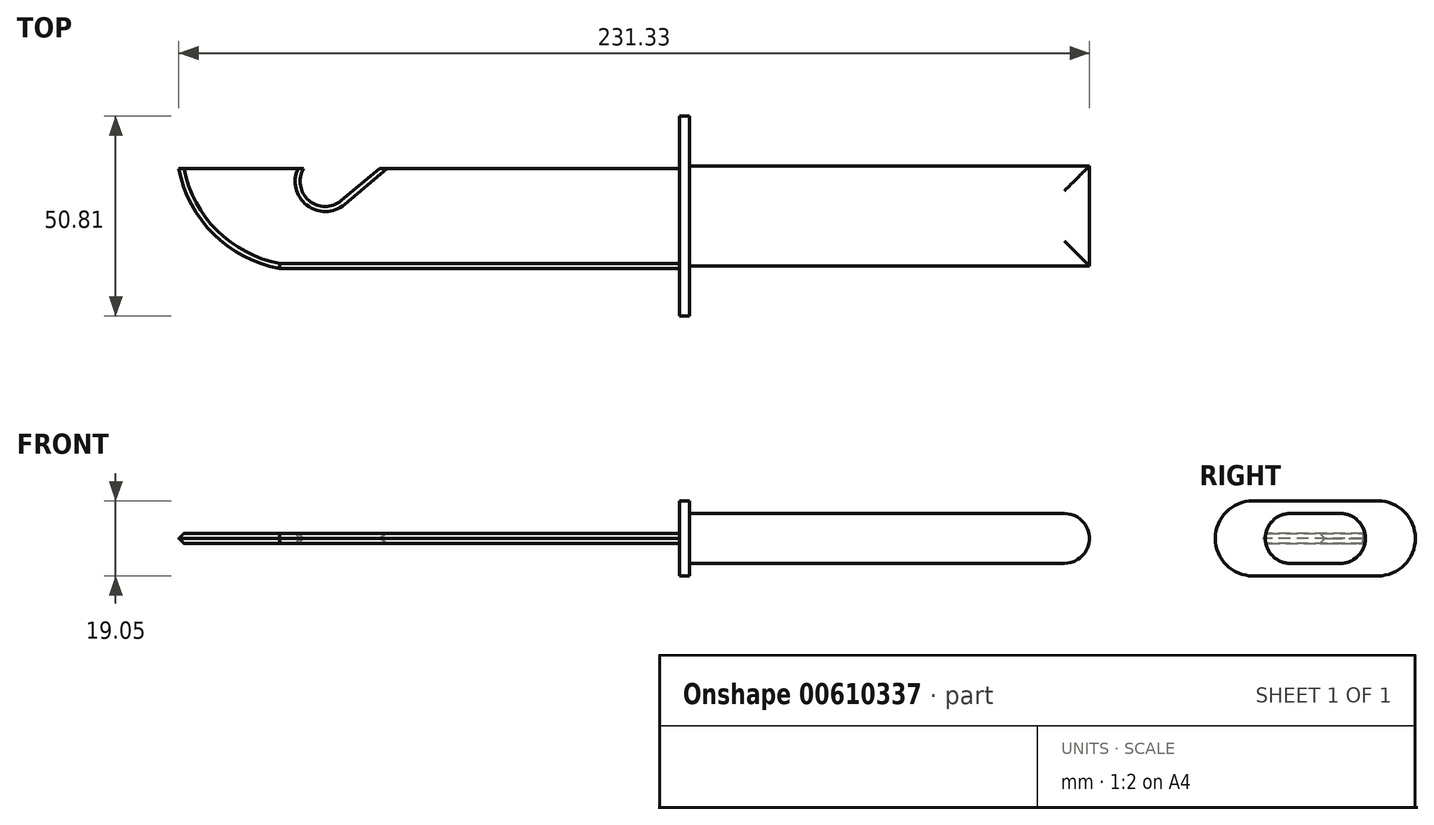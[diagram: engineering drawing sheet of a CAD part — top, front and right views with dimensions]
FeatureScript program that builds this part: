
annotation { "Feature Type Name" : "Feature", "Feature Type Description" : "" }
export const myFeature = defineFeature(function(context is Context, id is Id, definition is map)
    precondition{}
    {
        {
            var Q0;
            Q0=qCreatedBy(makeId("Top.planeOp"),FACE);
            var sketch = newSketch(context, id + "F0", { "sketchPlane" : qUnion([Q0])});
            skLineSegment(sketch, "E0", {"start": v(0, 0) * mm, "end": v(31.75, 0) * mm});
            skArc(sketch, "E1", {"start": v(31.75, 0) * mm, "mid": v(33.04, -8.12) * mm, "end": v(41.26, -8.16) * mm});
            skLineSegment(sketch, "E2", {"start": v(41.26, -8.16) * mm, "end": v(50.99, 0) * mm});
            skArc(sketch, "E3", {"start": v(0, 0) * mm, "mid": v(8.84, -16.68) * mm, "end": v(25.59, -25.4) * mm});
            skLineSegment(sketch, "E4", {"start": v(25.59, -25.4) * mm, "end": v(127.19, -25.4) * mm});
            skLineSegment(sketch, "E5", {"start": v(127.19, -25.4) * mm, "end": v(127.19, 0) * mm});
            skLineSegment(sketch, "E6", {"start": v(127.19, 0) * mm, "end": v(50.99, 0) * mm});
            skSolve(sketch);
        }
        {
            var Q0;
            Q0 = qSketchRegion(id + "F0", true);
            extrude(context, id + "F1", {"entities" : qUnion([Q0]), "depth" : 2.54 * mm, "offsetDistance" : 25.4 * mm});
        }
        {
            var Q0;
            Q0=makeQuery(id+"F1.opExtrude","CAP_EDGE",EDGE,{"disambiguationData":[OSD([sQuery(id+"F0.wireOp",EDGE,"E3")])],"isStart":false});
            var Q1;
            Q1=makeQuery(id+"F1.opExtrude","CAP_EDGE",EDGE,{"disambiguationData":[OSD([sQuery(id+"F0.wireOp",EDGE,"E4")])],"isStart":false});
            var Q2;
            Q2=makeQuery(id+"F1.opExtrude","CAP_EDGE",EDGE,{"disambiguationData":[OSD([sQuery(id+"F0.wireOp",EDGE,"E4")])],"isStart":true});
            var Q3;
            Q3=makeQuery(id+"F1.opExtrude","CAP_EDGE",EDGE,{"disambiguationData":[OSD([sQuery(id+"F0.wireOp",EDGE,"E3")])],"isStart":true});
            chamfer(context, id + "F2", {"entities" : qUnion([Q0, Q1, Q2, Q3]), "width" : 1.27 * mm, "tangentPropagation" : true});
        }
        {
            var Q0;
            Q0=makeQuery(id+"F1.opExtrude","CAP_EDGE",EDGE,{"disambiguationData":[OSD([sQuery(id+"F0.wireOp",EDGE,"E1")])],"isStart":true});
            var Q1;
            Q1=makeQuery(id+"F1.opExtrude","CAP_EDGE",EDGE,{"disambiguationData":[OSD([sQuery(id+"F0.wireOp",EDGE,"E1")])],"isStart":false});
            var Q2;
            Q2=makeQuery(id+"F1.opExtrude","CAP_EDGE",EDGE,{"disambiguationData":[OSD([sQuery(id+"F0.wireOp",EDGE,"E2")])],"isStart":true});
            var Q3;
            Q3=makeQuery(id+"F1.opExtrude","CAP_EDGE",EDGE,{"disambiguationData":[OSD([sQuery(id+"F0.wireOp",EDGE,"E2")])],"isStart":false});
            chamfer(context, id + "F3", {"entities" : qUnion([Q0, Q1, Q2, Q3]), "width" : 1.27 * mm, "tangentPropagation" : true});
        }
        {
            var Q0;
            Q0=makeQuery(id+"F1.opExtrude","SWEPT_FACE",FACE,{"disambiguationData":[OSD([sQuery(id+"F0.wireOp",EDGE,"E5")])]});
            var sketch = newSketch(context, id + "F4", { "sketchPlane" : qUnion([Q0])});
            skLineSegment(sketch, "E7.bottom", {"start": v(3.8, 10.8) * mm, "end": v(-27.94, 10.8) * mm});
            skLineSegment(sketch, "E7.top", {"start": v(3.8, -8.26) * mm, "end": v(-27.94, -8.26) * mm});
            skLineSegment(sketch, "E7.left", {"start": v(3.8, 10.8) * mm, "end": v(3.8, -8.26) * mm});
            skLineSegment(sketch, "E7.right", {"start": v(-27.94, 10.8) * mm, "end": v(-27.94, -8.26) * mm});
            skArc(sketch, "E8", {"start": v(3.8, -8.25) * mm, "mid": v(13.33, 1.27) * mm, "end": v(3.8, 10.8) * mm});
            skArc(sketch, "E9", {"start": v(-27.94, 10.8) * mm, "mid": v(-37.46, 1.27) * mm, "end": v(-27.94, -8.26) * mm});
            skSolve(sketch);
        }
        {
            var Q0;
            Q0 = qSketchRegion(id + "F4", true);
            extrude(context, id + "F5", {"entities" : qUnion([Q0]), "operationType" : NewBodyOperationType.ADD, "depth" : 2.54 * mm, "offsetDistance" : 25.4 * mm});
        }
        {
            var Q0;
            Q0=makeQuery(id+"F5.opExtrude","CAP_FACE",FACE,{"disambiguationData":[OSD([sQuery(id+"F4.wireOp",EDGE,"E7.bottom"),sQuery(id+"F4.wireOp",EDGE,"E7.top"),sQuery(id+"F4.wireOp",EDGE,"E8"),sQuery(id+"F4.wireOp",EDGE,"E9")])],"isStart":false});
            var sketch = newSketch(context, id + "F6", { "sketchPlane" : qUnion([Q0])});
            skLineSegment(sketch, "E10.bottom", {"start": v(-24.77, 7.62) * mm, "end": v(0.63, 7.62) * mm});
            skLineSegment(sketch, "E10.top", {"start": v(-24.77, -5.08) * mm, "end": v(0.63, -5.08) * mm});
            skLineSegment(sketch, "E10.left", {"start": v(-24.77, 7.62) * mm, "end": v(-24.77, -5.08) * mm});
            skLineSegment(sketch, "E10.right", {"start": v(0.63, 7.62) * mm, "end": v(0.63, -5.08) * mm});
            skSolve(sketch);
        }
        {
            var Q0;
            Q0 = qSketchRegion(id + "F6", true);
            extrude(context, id + "F7", {"entities" : qUnion([Q0]), "operationType" : NewBodyOperationType.ADD, "depth" : 101.6 * mm, "offsetDistance" : 25.4 * mm});
        }
        {
            var Q0;
            Q0=makeQuery(id+"F7.opExtrude","SWEPT_EDGE",EDGE,{"disambiguationData":[OSD([sQuery(id+"F6.wireOp",EDGE,"E10.bottom"),sQuery(id+"F6.wireOp",EDGE,"E10.right")])]});
            var Q1;
            Q1=makeQuery(id+"F7.opExtrude","SWEPT_EDGE",EDGE,{"disambiguationData":[OSD([sQuery(id+"F6.wireOp",EDGE,"E10.top"),sQuery(id+"F6.wireOp",EDGE,"E10.right")])]});
            var Q2;
            Q2=makeQuery(id+"F7.opExtrude","SWEPT_EDGE",EDGE,{"disambiguationData":[OSD([sQuery(id+"F6.wireOp",EDGE,"E10.top"),sQuery(id+"F6.wireOp",EDGE,"E10.left")])]});
            var Q3;
            Q3=makeQuery(id+"F7.opExtrude","SWEPT_EDGE",EDGE,{"disambiguationData":[OSD([sQuery(id+"F6.wireOp",EDGE,"E10.bottom"),sQuery(id+"F6.wireOp",EDGE,"E10.left")])]});
            var Q4;
            Q4=makeQuery(id+"F7.opExtrude","CAP_EDGE",EDGE,{"disambiguationData":[OSD([sQuery(id+"F6.wireOp",EDGE,"E10.bottom")])],"isStart":false});
            var Q5;
            Q5=makeQuery(id+"F7.opExtrude","CAP_EDGE",EDGE,{"disambiguationData":[OSD([sQuery(id+"F6.wireOp",EDGE,"E10.top")])],"isStart":false});
            fillet(context, id + "F8", {"entities" : qUnion([Q0, Q1, Q2, Q3, Q4, Q5]), "radius" : 6.35 * mm, "tangentPropagation" : true, "allowEdgeOverflow" : false});
        }
    });
